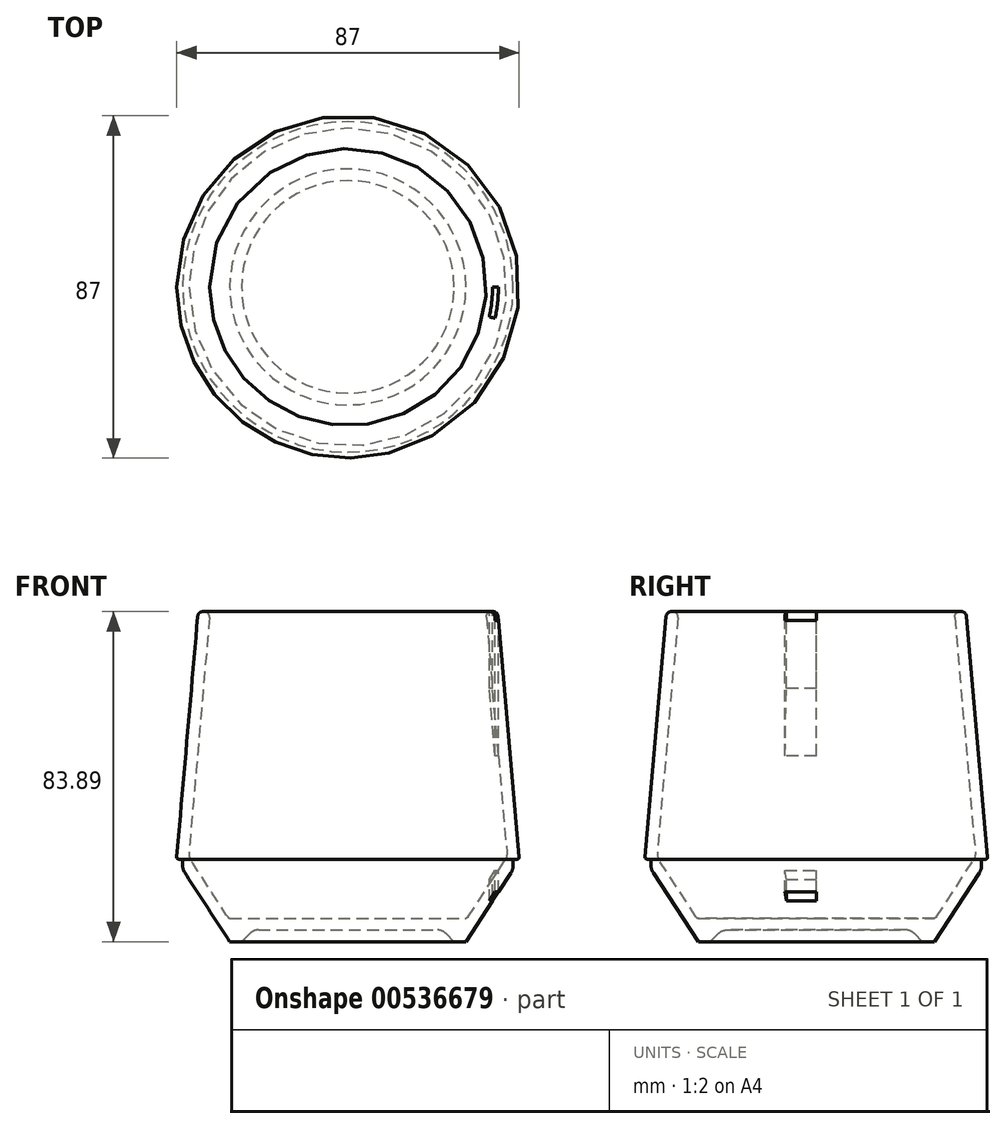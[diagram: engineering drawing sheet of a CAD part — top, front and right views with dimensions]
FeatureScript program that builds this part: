
annotation { "Feature Type Name" : "Feature", "Feature Type Description" : "" }
export const myFeature = defineFeature(function(context is Context, id is Id, definition is map)
    precondition{}
    {
        {
            var Q0;
            Q0=qCreatedBy(makeId("Front.planeOp"),FACE);
            var sketch = newSketch(context, id + "F0", { "sketchPlane" : qUnion([Q0])});
            skLineSegment(sketch, "E0", {"start": v(0, 3) * mm, "end": v(22.76, 3) * mm});
            skLineSegment(sketch, "E1", {"start": v(24.88, 2.12) * mm, "end": v(27, 0) * mm});
            skLineSegment(sketch, "E2", {"start": v(27, 0) * mm, "end": v(30, 0) * mm});
            skLineSegment(sketch, "E3", {"start": v(30, 0) * mm, "end": v(41.4, 17.5) * mm});
            skLineSegment(sketch, "E4", {"start": v(43.57, 20.72) * mm, "end": v(38.15, 82.7) * mm});
            skLineSegment(sketch, "E5", {"start": v(36.74, 83.89) * mm, "end": v(36.34, 83.85) * mm});
            skLineSegment(sketch, "E6", {"start": v(35.16, 82.44) * mm, "end": v(40.37, 22.84) * mm});
            skLineSegment(sketch, "E7", {"start": v(39.8, 20.52) * mm, "end": v(30.5, 6.28) * mm});
            skLineSegment(sketch, "E8", {"start": v(30, 6) * mm, "end": v(0, 6) * mm});
            skLineSegment(sketch, "E9", {"start": v(0, 6) * mm, "end": v(0, 3) * mm});
            skPoint(sketch, "E10.visualSharp", {"position": v(24, 3) * mm});
            skArc(sketch, "E10.filletArc", {"start": v(24.88, 2.12) * mm, "mid": v(23.9, 2.77) * mm, "end": v(22.76, 3) * mm});
            skPoint(sketch, "E11.visualSharp", {"position": v(30.33, 6) * mm});
            skArc(sketch, "E11.filletArc", {"start": v(30, 6) * mm, "mid": v(30.3, 6.07) * mm, "end": v(30.5, 6.28) * mm});
            skPoint(sketch, "E12.visualSharp", {"position": v(40.49, 21.58) * mm});
            skArc(sketch, "E12.filletArc", {"start": v(39.8, 20.52) * mm, "mid": v(40.28, 21.63) * mm, "end": v(40.37, 22.84) * mm});
            skArc(sketch, "E13.filletArc", {"start": v(41.4, 17.5) * mm, "mid": v(41.85, 18.46) * mm, "end": v(42, 19.5) * mm});
            skPoint(sketch, "E14.visualSharp", {"position": v(38.04, 84) * mm});
            skArc(sketch, "E14.filletArc", {"start": v(38.15, 82.7) * mm, "mid": v(37.69, 83.59) * mm, "end": v(36.74, 83.89) * mm});
            skPoint(sketch, "E15.visualSharp", {"position": v(35.05, 83.74) * mm});
            skArc(sketch, "E15.filletArc", {"start": v(36.34, 83.85) * mm, "mid": v(35.46, 83.4) * mm, "end": v(35.16, 82.44) * mm});
            skLineSegment(sketch, "E16", {"start": v(0, 0) * mm, "end": v(0, 82.7) * mm, "construction": true});
            skLineSegment(sketch, "E17", {"start": v(42, 19.5) * mm, "end": v(42, 20.5) * mm});
            skArc(sketch, "E18", {"start": v(43, 21) * mm, "mid": v(43.37, 21.16) * mm, "end": v(43.5, 21.54) * mm});
            skLineSegment(sketch, "E19", {"start": v(43, 21) * mm, "end": v(42.5, 21) * mm});
            skArc(sketch, "E20", {"start": v(42.5, 21) * mm, "mid": v(42.15, 20.85) * mm, "end": v(42, 20.5) * mm});
            skLineSegment(sketch, "E21", {"start": v(43.57, 0) * mm, "end": v(43.57, 82.7) * mm, "construction": true});
            skLineSegment(sketch, "E22", {"start": v(43.57, 20.72) * mm, "end": v(37.47, 90.45) * mm, "construction": true});
            skSolve(sketch);
        }
        {
            var Q0;
            Q0=qSketchRegion(id+"F0",true);
            var Q1;
            Q1=sQuery(id+"F0.wireOp",EDGE,"E16");
            revolve(context, id + "F1", {"entities" : qUnion([Q0]), "axis" : qUnion([Q1]), "revolveType" : RevolveType.FULL});
        }
        {
            var Q0;
            Q0=sQuery(id+"F0.wireOp",VERTEX,"E14.visualSharp");
            var Q1;
            Q1=qCreatedBy(makeId("Top.planeOp"),FACE);
            cPlane(context, id + "F2", {"entities" : qUnion([Q0, Q1]), "cplaneType" : CPlaneType.PLANE_POINT, "offset" : 25 * mm, "width" : 150 * mm, "height" : 150 * mm});
        }
        {
            var Q0;
            Q0=qCreatedBy(id+"F2.planeOp",FACE);
            var sketch = newSketch(context, id + "F3", { "sketchPlane" : qUnion([Q0])});
            skLineSegment(sketch, "E23", {"start": v(0, 0) * mm, "end": v(36.74, 0) * mm, "construction": true});
            skLineSegment(sketch, "E24", {"start": v(0, 0) * mm, "end": v(35.94, -7.64) * mm, "construction": true});
            skArc(sketch, "E25", {"start": v(36.74, 0) * mm, "mid": v(36.54, -3.84) * mm, "end": v(35.94, -7.64) * mm});
            skLineSegment(sketch, "E26", {"start": v(36.74, 0) * mm, "end": v(38.24, 0) * mm});
            skLineSegment(sketch, "E27", {"start": v(35.94, -7.64) * mm, "end": v(37.4, -7.95) * mm});
            skArc(sketch, "E28", {"start": v(38.24, 0) * mm, "mid": v(38.03, -4) * mm, "end": v(37.4, -7.95) * mm});
            skSolve(sketch);
        }
        {
            var Q0;
            Q0=qCreatedBy(makeId("Top.planeOp"),FACE);
            var Q1;
            Q1=sQuery(id+"F0.wireOp",VERTEX,"E18.start");
            cPlane(context, id + "F4", {"entities" : qUnion([Q0, Q1]), "cplaneType" : CPlaneType.PLANE_POINT, "offset" : 25 * mm, "width" : 150 * mm, "height" : 150 * mm});
        }
        {
            var Q0;
            Q0 = qSketchRegion(id + "F3", true);
            extrude(context, id + "F5", {"entities" : qUnion([Q0]), "operationType" : NewBodyOperationType.REMOVE, "oppositeDirection" : true, "depth" : 90 * mm, "offsetDistance" : 25 * mm});
        }
    });
